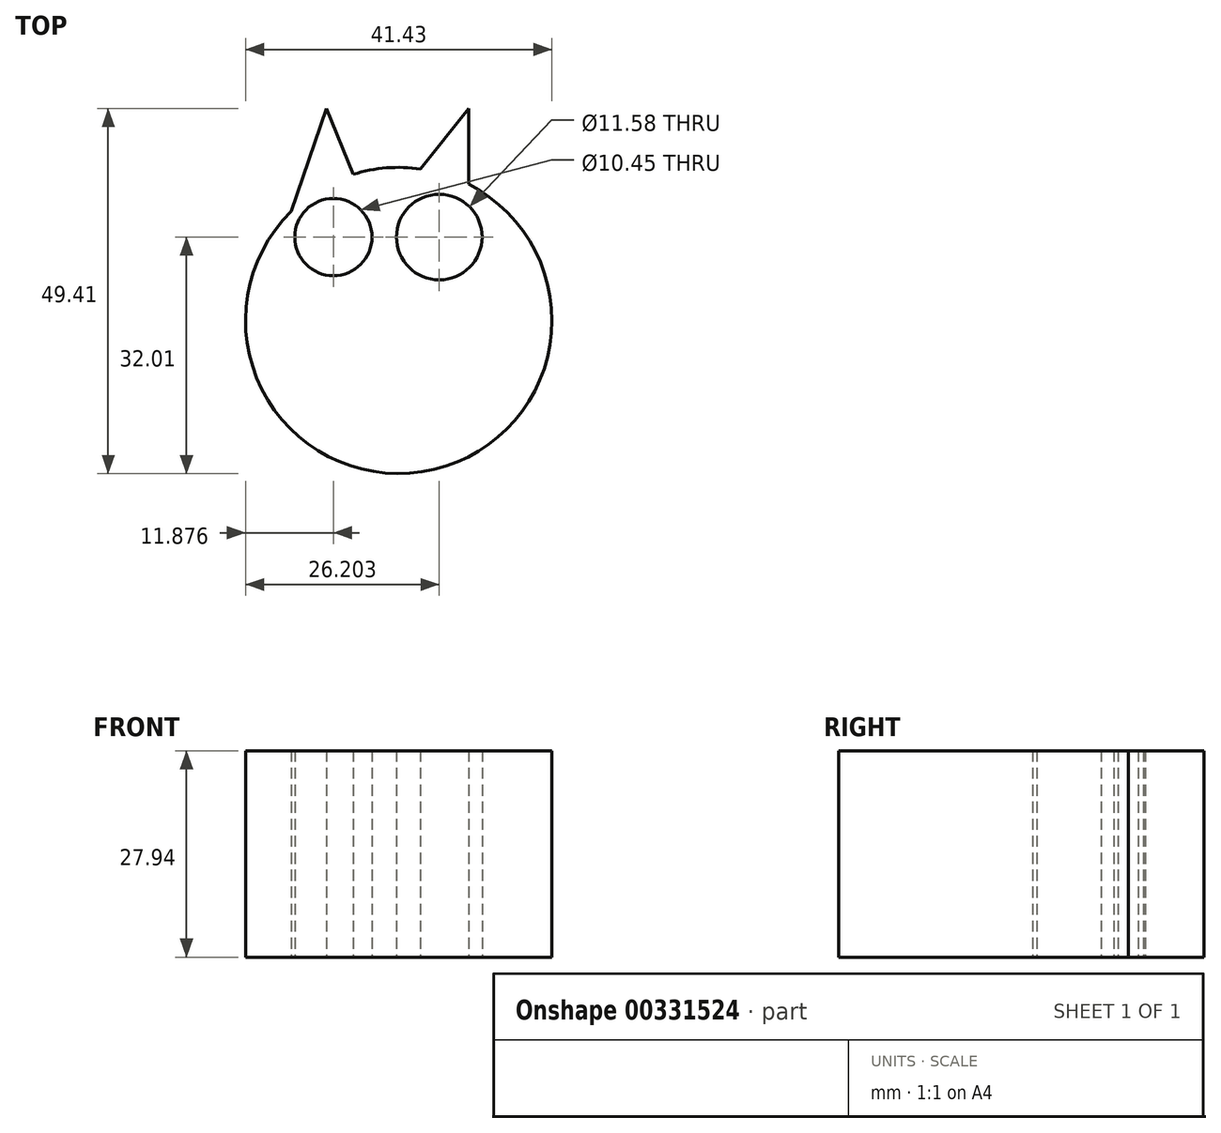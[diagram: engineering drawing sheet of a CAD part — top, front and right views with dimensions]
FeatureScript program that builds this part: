
annotation { "Feature Type Name" : "Feature", "Feature Type Description" : "" }
export const myFeature = defineFeature(function(context is Context, id is Id, definition is map)
    precondition{}
    {
        {
            var Q0;
            Q0=qCreatedBy(makeId("Top.planeOp"),FACE);
            var sketch = newSketch(context, id + "F0", { "sketchPlane" : qUnion([Q0])});
            skCircle(sketch, "E0", {"center": v(-23.77, 32.47) * mm, "radius": 20.72 * mm});
            skLineSegment(sketch, "E1", {"start": v(-38.31, 47.23) * mm, "end": v(-33.53, 61.16) * mm});
            skLineSegment(sketch, "E2", {"start": v(-33.53, 61.16) * mm, "end": v(-29.94, 52.25) * mm});
            skLineSegment(sketch, "E3", {"start": v(-20.85, 52.98) * mm, "end": v(-14.32, 61.16) * mm});
            skLineSegment(sketch, "E4", {"start": v(-14.32, 61.16) * mm, "end": v(-14.32, 50.91) * mm});
            skCircle(sketch, "E5", {"center": v(-32.61, 43.76) * mm, "radius": 5.22 * mm});
            skCircle(sketch, "E6", {"center": v(-18.29, 43.76) * mm, "radius": 5.79 * mm});
            skLineSegment(sketch, "E7", {"start": v(-27.39, 43.76) * mm, "end": v(-24.08, 43.76) * mm});
            skLineSegment(sketch, "E8", {"start": v(-24.08, 43.76) * mm, "end": v(-27.39, 43.76) * mm});
            skFitSpline(sketch, "E9", {"points": [v(-32.3, 26.97) * mm, v(-31.7, 20.26) * mm, v(-26.82, 16.3) * mm, v(-22.47, 11.8) * mm, v(-18.6, 19.05) * mm, v(-15.54, 24.24) * mm, v(-15.54, 24.24) * mm, v(-15.85, 29.43) * mm, v(-19.5, 30.95) * mm, v(-23.77, 23.93) * mm, v(-27.74, 29.11) * mm, v(-32.3, 26.97) * mm]});
            skPoint(sketch, "E10.1.internal.orphan", {"position": v(-34.44, 0) * mm});
            skFitSpline(sketch, "E11", {"points": [v(-32.3, 13.6) * mm, v(-34.44, 0) * mm, v(-34.44, -5.07) * mm, v(-32.3, -13) * mm, v(-20.42, -19.4) * mm, v(-6.7, -19.1) * mm, v(9.76, -17.56) * mm, v(22.56, -16.94) * mm, v(31.4, -17.54) * mm, v(65.23, -12.94) * mm, v(64.93, -10.8) * mm, v(64.02, -8.67) * mm, v(62.5, -3.79) * mm, v(60.66, 2.92) * mm, v(59.14, 5.37) * mm, v(57, 2.62) * mm, v(54.87, 0) * mm, v(54.26, -4.1) * mm, v(48.47, -9.9) * mm, v(42.37, -9.9) * mm, v(36.89, -9) * mm, v(27.74, -6.56) * mm, v(25.91, -5.64) * mm, v(17.38, -3.51) * mm, v(3.05, 0) * mm, v(3.05, 0) * mm, v(0, 0) * mm, v(-13.1, 2.57) * mm, v(-17.98, 9.28) * mm, v(-17.5, 12.73) * mm], "startDerivative": vector(-47.39, -317.34) * mm, "endDerivative": vector(61.64, 163.4) * mm});
            skFitSpline(sketch, "E12", {"points": [v(-34.44, 0) * mm, v(-42.06, -7.83) * mm, v(-34.44, -5.07) * mm], "startDerivative": vector(-22.42, -20.08) * mm, "endDerivative": vector(23.56, 10.7) * mm});
            skPoint(sketch, "E13.2.internal.orphan", {"position": v(-34.44, -15.76) * mm});
            skPoint(sketch, "E13.3.internal.orphan", {"position": v(-34.44, -16.06) * mm});
            skPoint(sketch, "E14.2.internal.orphan", {"position": v(-13.65, 2.92) * mm});
            skSolve(sketch);
        }
        {
            var Q0;
            Q0 = qSketchRegion(id + "F0", true);
            extrude(context, id + "F1", {"entities" : qUnion([Q0]), "depth" : 27.94 * mm, "hasSecondDirection" : true, "secondDirectionOppositeDirection" : false, "secondDirectionDepth" : 0 * mm});
        }
    });
